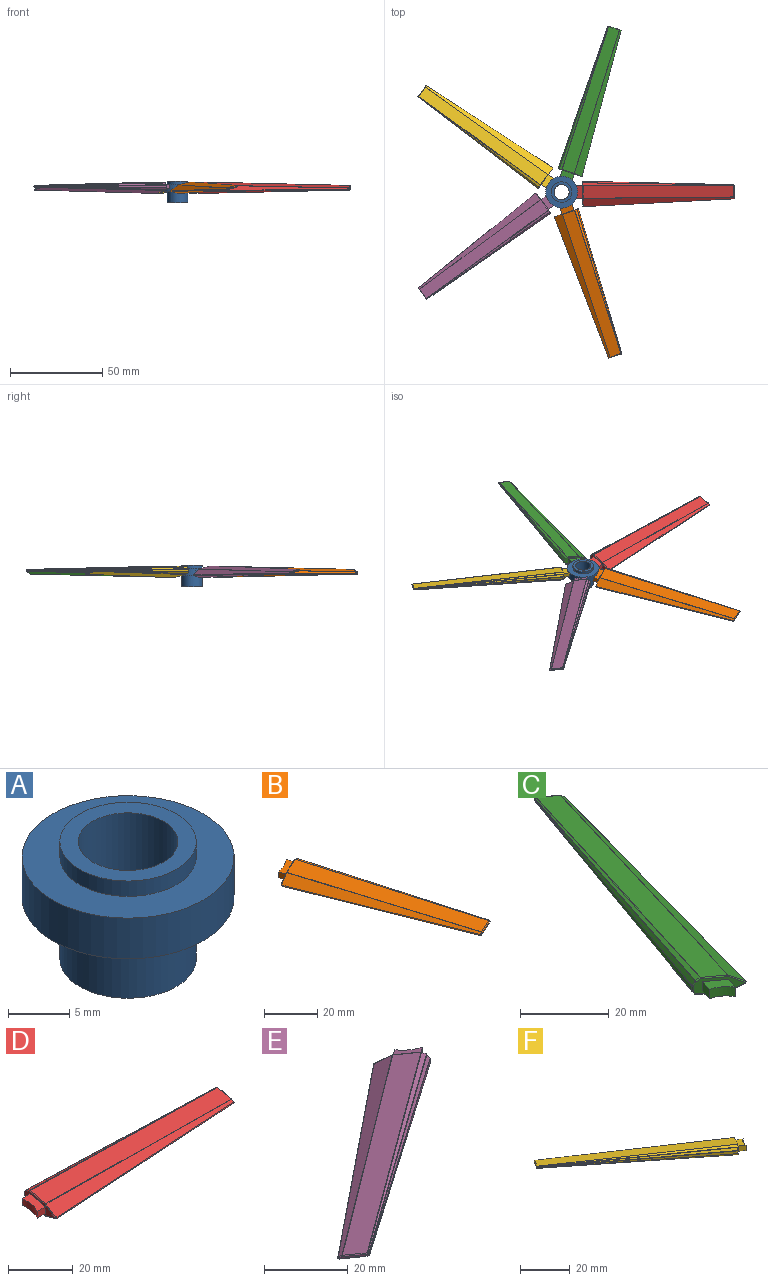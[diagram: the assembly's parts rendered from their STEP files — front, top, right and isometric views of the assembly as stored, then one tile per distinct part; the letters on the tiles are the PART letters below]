
ASSEMBLY  parts=6 mates=5
PART A: 8 faces, bbox 17.3x17.3x11.7 mm
  f0: cylinder r=5.56mm len=11.11mm, axis (0,0,-1), area 212.8mm2, adj f3,f6
  f1: cylinder r=5.56mm len=11.11mm, axis (0,0,-1), area 53.2mm2, adj f2,f7
  f2: plane 11.11x11.11mm, normal (0,0,1), area 45.1mm2, adj f1,f4
  f3: plane 11.11x11.11mm, normal (0,0,-1), area 45.1mm2, adj f0,f4
  f4: cylinder r=4.06mm len=11.68mm, axis (0,0,1), area 298.3mm2, adj f2,f3
  f5: cylinder r=8.64mm len=17.27mm, axis (0,0,1), area 220.5mm2, adj f6,f7
  f6: plane 17.27x17.27mm, normal (0,0,-1), area 137.3mm2, adj f0,f5
  f7: plane 17.27x17.27mm, normal (0,0,1), area 137.3mm2, adj f1,f5
PART B: 57 faces, bbox 36.5x83.4x6.3 mm
  f0: cylinder r=8.64mm len=6.36mm, axis (0,0,1), area 17.4mm2, adj f1,f2,f3,f4
  f1: plane 7.45x5.38mm, normal (-0.21,-0.07,0.97), area 20.7mm2, adj f0,f2,f4,f16
  f2: plane 3.3x2.54mm, normal (-0.95,-0.31,0), area 8.8mm2, adj f0,f1,f3,f16
  f3: plane 7.45x5.38mm, normal (0.21,0.07,-0.97), area 20.7mm2, adj f0,f2,f4,f16
  f4: plane 3.3x2.54mm, normal (0.95,0.31,0), area 8.8mm2, adj f0,f1,f3,f16
  f5: plane 78.08x25.36mm, normal (0.3,0.07,-0.95), area 81.9mm2, adj f19,f25,f28,f29
  f6: plane 78.11x24.21mm, normal (0.78,0.23,-0.59), area 55.6mm2, adj f18,f19,f21,f22
  f7: plane 78.09x23.5mm, normal (0.96,0.29,0), area 55.6mm2, adj f22,f23,f30,f31
  f8: plane 78.11x24.21mm, normal (0.78,0.23,0.59), area 55.6mm2, adj f31,f32,f37,f38
  f9: plane 77.94x25.3mm, normal (0.3,0.07,0.95), area 60.2mm2, adj f38,f39,f45,f46
  f10: plane 79.44x31.65mm, normal (-0.2,-0.09,0.97), area 540.6mm2, adj f46,f47,f51,f52
  f11: plane 77.59x29.99mm, normal (-0.53,-0.2,0.82), area 262.3mm2, adj f12,f41,f48,f52,f54
  f12: cone r=0.31mm half-angle=1.3deg, axis (-0.31,0.95,0), area 1.5mm2, adj f11,f13,f41,f55
  f13: plane 77.58x29.26mm, normal (-0.22,-0.1,-0.97), area 188.6mm2, adj f12,f14,f40,f41,f56
  f14: plane 79.73x31.38mm, normal (0.22,0.05,-0.97), area 564.5mm2, adj f13,f16,f25,f29,f36,f56
  f15: plane 6.84x2.22mm, normal (0.31,-0.95,0), area 3mm2, adj f18,f23,f28,f32,f36,f39,f40,f47
  f16: plane 12.51x5.82mm, normal (-0.31,0.95,0), area 27.8mm2, adj f1,f2,f3,f4,f14,f21,f25,f30
  f17: sphere r=0.25mm, area 0mm2, adj f18,f22,f23
  f18: cylinder r=0.25mm len=0.32mm, axis (-0.56,-0.18,-0.81), area 0mm2, adj f6,f15,f17,f24
  f19: cylinder r=0.25mm len=77.92mm, axis (-0.3,0.95,-0.02), area 13mm2, adj f5,f6,f20,f24
  f20: sphere r=0.25mm, area 0mm2, adj f19,f21,f25
  f21: cylinder r=0.25mm len=1.17mm, axis (0.56,0.18,0.81), area 0.5mm2, adj f6,f16,f20,f26
  f22: cylinder r=0.25mm len=78.11mm, axis (-0.29,0.96,-0.01), area 13mm2, adj f6,f7,f17,f26
  f23: cylinder r=0.25mm len=0.31mm, axis (0,0,-1), area 0mm2, adj f7,f15,f17,f27
  f24: sphere r=0.25mm, area 0mm2, adj f18,f19,f28
  f25: cylinder r=0.25mm len=3.97mm, axis (0.9,0.29,0.31), area 1mm2, adj f5,f14,f16,f20,f29
  f26: sphere r=0.25mm, area 0mm2, adj f21,f22,f30
  f27: sphere r=0.25mm, area 0mm2, adj f23,f31,f32
  f28: cylinder r=0.25mm len=0.64mm, axis (-0.9,-0.29,-0.31), area 0.3mm2, adj f5,f15,f24,f33
  f29: cylinder r=0.25mm len=77.72mm, axis (-0.3,0.95,-0.02), area 1.9mm2, adj f5,f14,f25,f33
  f30: cylinder r=0.25mm len=1.26mm, axis (0,0,1), area 0.5mm2, adj f7,f16,f26,f34
  f31: cylinder r=0.25mm len=78.11mm, axis (-0.29,0.96,0.01), area 13mm2, adj f7,f8,f27,f34
  f32: cylinder r=0.25mm len=0.32mm, axis (0.56,0.18,-0.81), area 0mm2, adj f8,f15,f27,f35
  f33: sphere r=0.25mm, area 0mm2, adj f28,f29,f36
  f34: sphere r=0.25mm, area 0mm2, adj f30,f31,f37
  f35: sphere r=0.25mm, area 0mm2, adj f32,f38,f39
  f36: cylinder r=0.25mm len=6.21mm, axis (0.93,0.3,0.22), area 2.6mm2, adj f14,f15,f33,f40
  f37: cylinder r=0.25mm len=1.17mm, axis (-0.56,-0.18,0.81), area 0.5mm2, adj f8,f16,f34,f42
  f38: cylinder r=0.25mm len=77.92mm, axis (-0.3,0.95,0.02), area 13mm2, adj f8,f9,f35,f42
  f39: cylinder r=0.25mm len=0.32mm, axis (0.9,0.29,-0.31), area 0.1mm2, adj f9,f15,f35,f43
  f40: cylinder r=0.25mm len=0.28mm, axis (0.92,0.3,-0.24), area 0mm2, adj f13,f15,f36,f44
  f41: cylinder r=0.25mm len=74.06mm, axis (-0.36,0.93,-0.01), area 46.2mm2, adj f11,f12,f13,f44
  f42: sphere r=0.25mm, area 0mm2, adj f37,f38,f45
  f43: sphere r=0.25mm, area 0mm2, adj f39,f46,f47
  f44: sphere r=0.25mm, area 0.1mm2, adj f40,f41,f48
  f45: cylinder r=0.25mm len=1.31mm, axis (-0.9,-0.29,0.31), area 0.5mm2, adj f9,f16,f42,f49
  f46: cylinder r=0.25mm len=77.61mm, axis (-0.31,0.95,0.02), area 11.1mm2, adj f9,f10,f43,f49
  f47: cylinder r=0.25mm len=5.89mm, axis (-0.93,-0.3,-0.22), area 2.4mm2, adj f10,f15,f43,f50
  f48: cylinder r=0.25mm len=1.06mm, axis (-0.78,-0.25,-0.57), area 0.4mm2, adj f11,f15,f44,f50
  f49: sphere r=0.25mm, area 0mm2, adj f45,f46,f51
  f50: sphere r=0.25mm, area 0mm2, adj f47,f48,f52
  f51: cylinder r=0.25mm len=6.58mm, axis (0.93,0.3,0.22), area 2.8mm2, adj f10,f16,f49,f53
  f52: cylinder r=0.25mm len=77.35mm, axis (-0.32,0.95,0.02), area 7.9mm2, adj f10,f11,f50,f53
  f53: sphere r=0.25mm, area 0mm2, adj f51,f52,f54
  f54: cylinder r=0.25mm len=4.18mm, axis (0.78,0.25,0.57), area 2.1mm2, adj f11,f16,f53,f55
  f55: torus R=0.05mm, axis (0.31,-0.95,0), area 0.2mm2, adj f12,f16,f54,f56
  f56: cylinder r=0.25mm len=4.56mm, axis (-0.92,-0.3,0.24), area 1.8mm2, adj f13,f14,f16,f55
PART C: 57 faces, bbox 34.3x83.6x6.3 mm
  f0: cylinder r=8.64mm len=6.36mm, axis (0,0,1), area 17.4mm2, adj f1,f2,f3,f4
  f1: plane 7.45x5.38mm, normal (0.21,-0.07,0.97), area 20.7mm2, adj f0,f2,f4,f16
  f2: plane 3.3x2.54mm, normal (0.95,-0.31,0), area 8.8mm2, adj f0,f1,f3,f16
  f3: plane 7.45x5.38mm, normal (-0.21,0.07,-0.97), area 20.7mm2, adj f0,f2,f4,f16
  f4: plane 3.3x2.54mm, normal (-0.95,0.31,0), area 8.8mm2, adj f0,f1,f3,f16
  f5: plane 77.6x26.85mm, normal (-0.29,0.12,-0.95), area 81.9mm2, adj f19,f25,f28,f29
  f6: plane 77.22x26.95mm, normal (-0.76,0.27,-0.59), area 55.6mm2, adj f18,f19,f21,f22
  f7: plane 76.99x26.89mm, normal (-0.94,0.33,0), area 55.6mm2, adj f22,f23,f30,f31
  f8: plane 77.22x26.95mm, normal (-0.76,0.27,0.59), area 55.6mm2, adj f31,f32,f37,f38
  f9: plane 77.58x26.43mm, normal (-0.29,0.12,0.95), area 60.2mm2, adj f38,f39,f45,f46
  f10: plane 79.64x31.03mm, normal (0.22,-0.05,0.97), area 540.6mm2, adj f46,f47,f51,f52
  f11: plane 79.1x25.34mm, normal (0.55,-0.15,0.82), area 262.3mm2, adj f12,f41,f48,f52,f54
  f12: cone r=0.31mm half-angle=1.3deg, axis (-0.31,-0.95,0), area 1.5mm2, adj f11,f13,f41,f55
  f13: plane 78.86x25.3mm, normal (0.24,-0.05,-0.97), area 188.6mm2, adj f12,f14,f40,f41,f56
  f14: plane 79.68x31.82mm, normal (-0.2,0.09,-0.97), area 564.5mm2, adj f13,f16,f25,f29,f36,f56
  f15: plane 6.84x2.22mm, normal (0.31,0.95,0), area 3mm2, adj f18,f23,f28,f32,f36,f39,f40,f47
  f16: plane 12.51x5.82mm, normal (-0.31,-0.95,0), area 27.8mm2, adj f1,f2,f3,f4,f14,f21,f25,f30
  f17: sphere r=0.25mm, area 0mm2, adj f18,f22,f23
  f18: cylinder r=0.25mm len=0.33mm, axis (0.56,-0.18,-0.81), area 0mm2, adj f6,f15,f17,f24
  f19: cylinder r=0.25mm len=77.24mm, axis (-0.32,-0.95,-0.02), area 13mm2, adj f5,f6,f20,f24
  f20: sphere r=0.25mm, area 0mm2, adj f19,f21,f25
  f21: cylinder r=0.25mm len=1.17mm, axis (-0.56,0.18,0.81), area 0.5mm2, adj f6,f16,f20,f26
  f22: cylinder r=0.25mm len=77.01mm, axis (-0.33,-0.94,-0.01), area 13mm2, adj f6,f7,f17,f26
  f23: cylinder r=0.25mm len=0.32mm, axis (0,0,-1), area 0mm2, adj f7,f15,f17,f27
  f24: sphere r=0.25mm, area 0mm2, adj f18,f19,f28
  f25: cylinder r=0.25mm len=3.85mm, axis (-0.9,0.29,0.31), area 1mm2, adj f5,f14,f16,f20,f29
  f26: sphere r=0.25mm, area 0mm2, adj f21,f22,f30
  f27: sphere r=0.25mm, area 0mm2, adj f23,f31,f32
  f28: cylinder r=0.25mm len=0.76mm, axis (0.9,-0.29,-0.31), area 0.3mm2, adj f5,f15,f24,f33
  f29: cylinder r=0.25mm len=77.43mm, axis (-0.31,-0.95,-0.02), area 1.9mm2, adj f5,f14,f25,f33
  f30: cylinder r=0.25mm len=1.26mm, axis (0,0,1), area 0.5mm2, adj f7,f16,f26,f34
  f31: cylinder r=0.25mm len=77.01mm, axis (-0.33,-0.94,0.01), area 13mm2, adj f7,f8,f27,f34
  f32: cylinder r=0.25mm len=0.33mm, axis (-0.56,0.18,-0.81), area 0mm2, adj f8,f15,f27,f35
  f33: sphere r=0.25mm, area 0mm2, adj f28,f29,f36
  f34: sphere r=0.25mm, area 0mm2, adj f30,f31,f37
  f35: sphere r=0.25mm, area 0mm2, adj f32,f38,f39
  f36: cylinder r=0.25mm len=6.3mm, axis (-0.93,0.3,0.22), area 2.6mm2, adj f14,f15,f33,f40
  f37: cylinder r=0.25mm len=1.17mm, axis (0.56,-0.18,0.81), area 0.5mm2, adj f8,f16,f34,f42
  f38: cylinder r=0.25mm len=77.24mm, axis (-0.32,-0.95,0.02), area 13mm2, adj f8,f9,f35,f42
  f39: cylinder r=0.25mm len=0.34mm, axis (-0.9,0.29,-0.31), area 0.1mm2, adj f9,f15,f35,f43
  f40: cylinder r=0.25mm len=0.29mm, axis (-0.92,0.3,-0.24), area 0mm2, adj f13,f15,f36,f44
  f41: cylinder r=0.25mm len=76.6mm, axis (-0.26,-0.97,-0.01), area 46.2mm2, adj f11,f12,f13,f44
  f42: sphere r=0.25mm, area 0mm2, adj f37,f38,f45
  f43: sphere r=0.25mm, area 0mm2, adj f39,f46,f47
  f44: sphere r=0.25mm, area 0.1mm2, adj f40,f41,f48
  f45: cylinder r=0.25mm len=1.19mm, axis (0.9,-0.29,0.31), area 0.5mm2, adj f9,f16,f42,f49
  f46: cylinder r=0.25mm len=77.56mm, axis (-0.31,-0.95,0.02), area 11.1mm2, adj f9,f10,f43,f49
  f47: cylinder r=0.25mm len=5.8mm, axis (0.93,-0.3,-0.22), area 2.4mm2, adj f10,f15,f43,f50
  f48: cylinder r=0.25mm len=0.92mm, axis (0.78,-0.25,-0.57), area 0.4mm2, adj f11,f15,f44,f50
  f49: sphere r=0.25mm, area 0mm2, adj f45,f46,f51
  f50: sphere r=0.25mm, area 0mm2, adj f47,f48,f52
  f51: cylinder r=0.25mm len=6.67mm, axis (-0.93,0.3,0.22), area 2.8mm2, adj f10,f16,f49,f53
  f52: cylinder r=0.25mm len=77.8mm, axis (-0.3,-0.95,0.02), area 7.9mm2, adj f10,f11,f50,f53
  f53: sphere r=0.25mm, area 0mm2, adj f51,f52,f54
  f54: cylinder r=0.25mm len=4.32mm, axis (-0.78,0.25,0.57), area 2.1mm2, adj f11,f16,f53,f55
  f55: torus R=0.05mm, axis (0.31,0.95,0), area 0.2mm2, adj f12,f16,f54,f56
  f56: cylinder r=0.25mm len=4.66mm, axis (0.92,-0.3,0.24), area 1.8mm2, adj f13,f14,f16,f55
PART D: 57 faces, bbox 85.5x13.7x6.3 mm
  f0: cylinder r=8.64mm len=6.69mm, axis (0,0,1), area 17.4mm2, adj f1,f2,f3,f4
  f1: plane 6.7x3.48mm, normal (0,-0.22,0.97), area 20.7mm2, adj f0,f2,f4,f16
  f2: plane 3.47x2.54mm, normal (0,-1,0), area 8.8mm2, adj f0,f1,f3,f16
  f3: plane 6.7x3.48mm, normal (0,0.22,-0.97), area 20.7mm2, adj f0,f2,f4,f16
  f4: plane 3.47x2.54mm, normal (0,1,0), area 8.8mm2, adj f0,f1,f3,f16
  f5: plane 81.53x1.93mm, normal (0.02,0.31,-0.95), area 81.9mm2, adj f19,f25,f28,f29
  f6: plane 81.53x1.84mm, normal (0.02,0.81,-0.59), area 55.6mm2, adj f18,f19,f21,f22
  f7: plane 81.53x1.78mm, normal (0.02,1,0), area 55.6mm2, adj f22,f23,f30,f31
  f8: plane 81.53x1.84mm, normal (0.02,0.81,0.59), area 55.6mm2, adj f31,f32,f37,f38
  f9: plane 81.53x1.91mm, normal (0.02,0.31,0.95), area 60.2mm2, adj f38,f39,f45,f46
  f10: plane 81.53x6.87mm, normal (0.02,-0.22,0.97), area 540.6mm2, adj f46,f47,f51,f52
  f11: plane 81.53x5.04mm, normal (0.02,-0.57,0.82), area 262.3mm2, adj f12,f41,f48,f52,f54
  f12: cone r=0.31mm half-angle=1.3deg, axis (-1,0,0), area 1.5mm2, adj f11,f13,f41,f55
  f13: plane 81.53x4.27mm, normal (0.02,-0.24,-0.97), area 188.6mm2, adj f12,f14,f40,f41,f56
  f14: plane 81.79x6.97mm, normal (0.02,0.22,-0.97), area 564.5mm2, adj f13,f16,f25,f29,f36,f56
  f15: plane 7.2x2.01mm, normal (1,0,0), area 3mm2, adj f18,f23,f28,f32,f36,f39,f40,f47
  f16: plane 13.16x5.82mm, normal (-1,0,0), area 27.8mm2, adj f1,f2,f3,f4,f14,f21,f25,f30
  f17: sphere r=0.25mm, area 0mm2, adj f18,f22,f23
  f18: cylinder r=0.25mm len=0.27mm, axis (0,-0.59,-0.81), area 0mm2, adj f6,f15,f17,f24
  f19: cylinder r=0.25mm len=81.53mm, axis (-1,0.01,-0.02), area 13mm2, adj f5,f6,f20,f24
  f20: sphere r=0.25mm, area 0mm2, adj f19,f21,f25
  f21: cylinder r=0.25mm len=1.17mm, axis (0,0.59,0.81), area 0.5mm2, adj f6,f16,f20,f26
  f22: cylinder r=0.25mm len=81.53mm, axis (-1,0.02,-0.01), area 13mm2, adj f6,f7,f17,f26
  f23: cylinder r=0.25mm len=0.25mm, axis (0,0,-1), area 0mm2, adj f7,f15,f17,f27
  f24: sphere r=0.25mm, area 0mm2, adj f18,f19,f28
  f25: cylinder r=0.25mm len=4.09mm, axis (0,0.95,0.31), area 1mm2, adj f5,f14,f16,f20,f29
  f26: sphere r=0.25mm, area 0mm2, adj f21,f22,f30
  f27: sphere r=0.25mm, area 0mm2, adj f23,f31,f32
  f28: cylinder r=0.25mm len=0.72mm, axis (0,-0.95,-0.31), area 0.3mm2, adj f5,f15,f24,f33
  f29: cylinder r=0.25mm len=81.56mm, axis (-1,0.01,-0.02), area 1.9mm2, adj f5,f14,f25,f33
  f30: cylinder r=0.25mm len=1.26mm, axis (0,0,1), area 0.5mm2, adj f7,f16,f26,f34
  f31: cylinder r=0.25mm len=81.53mm, axis (-1,0.02,0.01), area 13mm2, adj f7,f8,f27,f34
  f32: cylinder r=0.25mm len=0.27mm, axis (0,0.59,-0.81), area 0mm2, adj f8,f15,f27,f35
  f33: sphere r=0.25mm, area 0mm2, adj f28,f29,f36
  f34: sphere r=0.25mm, area 0mm2, adj f30,f31,f37
  f35: sphere r=0.25mm, area 0mm2, adj f32,f38,f39
  f36: cylinder r=0.25mm len=6.54mm, axis (0,0.97,0.22), area 2.6mm2, adj f14,f15,f33,f40
  f37: cylinder r=0.25mm len=1.17mm, axis (0,-0.59,0.81), area 0.5mm2, adj f8,f16,f34,f42
  f38: cylinder r=0.25mm len=81.53mm, axis (-1,0.01,0.02), area 13mm2, adj f8,f9,f35,f42
  f39: cylinder r=0.25mm len=0.3mm, axis (0,0.95,-0.31), area 0.1mm2, adj f9,f15,f35,f43
  f40: cylinder r=0.25mm len=0.28mm, axis (0,0.97,-0.24), area 0mm2, adj f13,f15,f36,f44
  f41: cylinder r=0.25mm len=79.15mm, axis (-1,-0.05,-0.01), area 46.2mm2, adj f11,f12,f13,f44
  f42: sphere r=0.25mm, area 0mm2, adj f37,f38,f45
  f43: sphere r=0.25mm, area 0mm2, adj f39,f46,f47
  f44: sphere r=0.25mm, area 0.1mm2, adj f40,f41,f48
  f45: cylinder r=0.25mm len=1.29mm, axis (0,-0.95,0.31), area 0.5mm2, adj f9,f16,f42,f49
  f46: cylinder r=0.25mm len=81.53mm, axis (-1,0,0.02), area 11.1mm2, adj f9,f10,f43,f49
  f47: cylinder r=0.25mm len=6.11mm, axis (0,-0.97,-0.22), area 2.4mm2, adj f10,f15,f43,f50
  f48: cylinder r=0.25mm len=1.03mm, axis (0,-0.82,-0.57), area 0.4mm2, adj f11,f15,f44,f50
  f49: sphere r=0.25mm, area 0mm2, adj f45,f46,f51
  f50: sphere r=0.25mm, area 0mm2, adj f47,f48,f52
  f51: cylinder r=0.25mm len=6.93mm, axis (0,0.97,0.22), area 2.8mm2, adj f10,f16,f49,f53
  f52: cylinder r=0.25mm len=81.53mm, axis (-1,-0.01,0.02), area 7.9mm2, adj f10,f11,f50,f53
  f53: sphere r=0.25mm, area 0mm2, adj f51,f52,f54
  f54: cylinder r=0.25mm len=4.46mm, axis (0,0.82,0.57), area 2.1mm2, adj f11,f16,f53,f55
  f55: torus R=0.05mm, axis (1,0,0), area 0.2mm2, adj f12,f16,f54,f56
  f56: cylinder r=0.25mm len=4.82mm, axis (0,-0.97,0.24), area 1.8mm2, adj f13,f14,f16,f55
PART E: 57 faces, bbox 73.2x57.7x6.3 mm
  f0: cylinder r=8.64mm len=5.41mm, axis (0,0,1), area 17.4mm2, adj f1,f2,f3,f4
  f1: plane 7.46x6.75mm, normal (-0.13,0.18,0.97), area 20.7mm2, adj f0,f2,f4,f16
  f2: plane 2.81x2.54mm, normal (-0.59,0.81,0), area 8.8mm2, adj f0,f1,f3,f16
  f3: plane 7.46x6.75mm, normal (0.13,-0.18,-0.97), area 20.7mm2, adj f0,f2,f4,f16
  f4: plane 2.81x2.54mm, normal (0.59,-0.81,0), area 8.8mm2, adj f0,f1,f3,f16
  f5: plane 66.99x48.06mm, normal (0.16,-0.26,-0.95), area 81.9mm2, adj f19,f25,f28,f29
  f6: plane 67.04x47.08mm, normal (0.46,-0.67,-0.59), area 55.6mm2, adj f18,f19,f21,f22
  f7: plane 67.01x46.49mm, normal (0.57,-0.82,0), area 55.6mm2, adj f22,f23,f30,f31
  f8: plane 67.04x47.08mm, normal (0.46,-0.67,0.59), area 55.6mm2, adj f31,f32,f37,f38
  f9: plane 66.72x48.01mm, normal (0.16,-0.26,0.95), area 60.2mm2, adj f38,f39,f45,f46
  f10: plane 69.57x53.41mm, normal (-0.15,0.17,0.97), area 540.6mm2, adj f46,f47,f51,f52
  f11: plane 66.05x52.01mm, normal (-0.35,0.45,0.82), area 262.3mm2, adj f12,f41,f48,f52,f54
  f12: cone r=0.31mm half-angle=1.3deg, axis (0.81,0.59,0), area 1.5mm2, adj f11,f13,f41,f55
  f13: plane 66.03x51.38mm, normal (-0.16,0.18,-0.97), area 188.6mm2, adj f12,f14,f40,f41,f56
  f14: plane 70.07x53.21mm, normal (0.11,-0.19,-0.97), area 564.5mm2, adj f13,f16,f25,f29,f36,f56
  f15: plane 5.82x4.23mm, normal (-0.81,-0.59,0), area 3mm2, adj f18,f23,f28,f32,f36,f39,f40,f47
  f16: plane 10.65x7.73mm, normal (0.81,0.59,0), area 27.8mm2, adj f1,f2,f3,f4,f14,f21,f25,f30
  f17: sphere r=0.25mm, area 0mm2, adj f18,f22,f23
  f18: cylinder r=0.25mm len=0.36mm, axis (-0.35,0.48,-0.81), area 0mm2, adj f6,f15,f17,f24
  f19: cylinder r=0.25mm len=66.68mm, axis (0.82,0.58,-0.02), area 13mm2, adj f5,f6,f20,f24
  f20: sphere r=0.25mm, area 0mm2, adj f19,f21,f25
  f21: cylinder r=0.25mm len=1.17mm, axis (0.35,-0.48,0.81), area 0.5mm2, adj f6,f16,f20,f26
  f22: cylinder r=0.25mm len=67.04mm, axis (0.82,0.57,-0.01), area 13mm2, adj f6,f7,f17,f26
  f23: cylinder r=0.25mm len=0.35mm, axis (0,0,-1), area 0mm2, adj f7,f15,f17,f27
  f24: sphere r=0.25mm, area 0mm2, adj f18,f19,f28
  f25: cylinder r=0.25mm len=3.46mm, axis (0.56,-0.77,0.31), area 1mm2, adj f5,f14,f16,f20,f29
  f26: sphere r=0.25mm, area 0mm2, adj f21,f22,f30
  f27: sphere r=0.25mm, area 0mm2, adj f23,f31,f32
  f28: cylinder r=0.25mm len=0.62mm, axis (-0.56,0.77,-0.31), area 0.3mm2, adj f5,f15,f24,f33
  f29: cylinder r=0.25mm len=66.27mm, axis (0.81,0.58,-0.02), area 1.9mm2, adj f5,f14,f25,f33
  f30: cylinder r=0.25mm len=1.26mm, axis (0,0,1), area 0.5mm2, adj f7,f16,f26,f34
  f31: cylinder r=0.25mm len=67.04mm, axis (0.82,0.57,0.01), area 13mm2, adj f7,f8,f27,f34
  f32: cylinder r=0.25mm len=0.36mm, axis (0.35,-0.48,-0.81), area 0mm2, adj f8,f15,f27,f35
  f33: sphere r=0.25mm, area 0mm2, adj f28,f29,f36
  f34: sphere r=0.25mm, area 0mm2, adj f30,f31,f37
  f35: sphere r=0.25mm, area 0mm2, adj f32,f38,f39
  f36: cylinder r=0.25mm len=5.35mm, axis (0.57,-0.79,0.22), area 2.6mm2, adj f14,f15,f33,f40
  f37: cylinder r=0.25mm len=1.17mm, axis (-0.35,0.48,0.81), area 0.5mm2, adj f8,f16,f34,f42
  f38: cylinder r=0.25mm len=66.68mm, axis (0.82,0.58,0.02), area 13mm2, adj f8,f9,f35,f42
  f39: cylinder r=0.25mm len=0.36mm, axis (0.56,-0.77,-0.31), area 0.1mm2, adj f9,f15,f35,f43
  f40: cylinder r=0.25mm len=0.3mm, axis (0.57,-0.79,-0.24), area 0mm2, adj f13,f15,f36,f44
  f41: cylinder r=0.25mm len=61.72mm, axis (0.78,0.63,-0.01), area 46.2mm2, adj f11,f12,f13,f44
  f42: sphere r=0.25mm, area 0mm2, adj f37,f38,f45
  f43: sphere r=0.25mm, area 0mm2, adj f39,f46,f47
  f44: sphere r=0.25mm, area 0.1mm2, adj f40,f41,f48
  f45: cylinder r=0.25mm len=1.2mm, axis (-0.56,0.77,0.31), area 0.5mm2, adj f9,f16,f42,f49
  f46: cylinder r=0.25mm len=66.09mm, axis (0.81,0.59,0.02), area 11.1mm2, adj f9,f10,f43,f49
  f47: cylinder r=0.25mm len=5.09mm, axis (-0.57,0.79,-0.22), area 2.4mm2, adj f10,f15,f43,f50
  f48: cylinder r=0.25mm len=0.98mm, axis (-0.48,0.67,-0.57), area 0.4mm2, adj f11,f15,f44,f50
  f49: sphere r=0.25mm, area 0mm2, adj f45,f46,f51
  f50: sphere r=0.25mm, area 0mm2, adj f47,f48,f52
  f51: cylinder r=0.25mm len=5.67mm, axis (0.57,-0.79,0.22), area 2.8mm2, adj f10,f16,f49,f53
  f52: cylinder r=0.25mm len=65.59mm, axis (0.8,0.59,0.02), area 7.9mm2, adj f10,f11,f50,f53
  f53: sphere r=0.25mm, area 0mm2, adj f51,f52,f54
  f54: cylinder r=0.25mm len=3.57mm, axis (0.48,-0.67,0.57), area 2.1mm2, adj f11,f16,f53,f55
  f55: torus R=0.05mm, axis (-0.81,-0.59,0), area 0.2mm2, adj f12,f16,f54,f56
  f56: cylinder r=0.25mm len=3.96mm, axis (-0.57,0.79,0.24), area 1.8mm2, adj f13,f14,f16,f55
PART F: 57 faces, bbox 73.4x55.8x6.3 mm
  f0: cylinder r=8.64mm len=5.41mm, axis (0,0,1), area 17.4mm2, adj f1,f2,f3,f4
  f1: plane 7.46x6.75mm, normal (0.13,0.18,0.97), area 20.7mm2, adj f0,f2,f4,f16
  f2: plane 2.81x2.54mm, normal (0.59,0.81,0), area 8.8mm2, adj f0,f1,f3,f16
  f3: plane 7.46x6.75mm, normal (-0.13,-0.18,-0.97), area 20.7mm2, adj f0,f2,f4,f16
  f4: plane 2.81x2.54mm, normal (-0.59,-0.81,0), area 8.8mm2, adj f0,f1,f3,f16
  f5: plane 66.06x49.33mm, normal (-0.2,-0.24,-0.95), area 81.9mm2, adj f19,f25,f28,f29
  f6: plane 65.35x49.41mm, normal (-0.49,-0.64,-0.59), area 55.6mm2, adj f18,f19,f21,f22
  f7: plane 64.92x49.36mm, normal (-0.61,-0.8,0), area 55.6mm2, adj f22,f23,f30,f31
  f8: plane 65.35x49.41mm, normal (-0.49,-0.64,0.59), area 55.6mm2, adj f31,f32,f37,f38
  f9: plane 66.03x48.97mm, normal (-0.2,-0.24,0.95), area 60.2mm2, adj f38,f39,f45,f46
  f10: plane 69.95x52.89mm, normal (0.11,0.19,0.97), area 540.6mm2, adj f46,f47,f51,f52
  f11: plane 68.93x48.05mm, normal (0.32,0.47,0.82), area 262.3mm2, adj f12,f41,f48,f52,f54
  f12: cone r=0.31mm half-angle=1.3deg, axis (0.81,-0.59,0), area 1.5mm2, adj f11,f13,f41,f55
  f13: plane 68.47x48.01mm, normal (0.12,0.21,-0.97), area 188.6mm2, adj f12,f14,f40,f41,f56
  f14: plane 69.84x53.57mm, normal (-0.15,-0.17,-0.97), area 564.5mm2, adj f13,f16,f25,f29,f36,f56
  f15: plane 5.82x4.23mm, normal (-0.81,0.59,0), area 3mm2, adj f18,f23,f28,f32,f36,f39,f40,f47
  f16: plane 10.65x7.73mm, normal (0.81,-0.59,0), area 27.8mm2, adj f1,f2,f3,f4,f14,f21,f25,f30
  f17: sphere r=0.25mm, area 0mm2, adj f18,f22,f23
  f18: cylinder r=0.25mm len=0.36mm, axis (0.35,0.48,-0.81), area 0mm2, adj f6,f15,f17,f24
  f19: cylinder r=0.25mm len=65.39mm, axis (0.8,-0.6,-0.02), area 13mm2, adj f5,f6,f20,f24
  f20: sphere r=0.25mm, area 0mm2, adj f19,f21,f25
  f21: cylinder r=0.25mm len=1.17mm, axis (-0.35,-0.48,0.81), area 0.5mm2, adj f6,f16,f20,f26
  f22: cylinder r=0.25mm len=64.95mm, axis (0.8,-0.61,-0.01), area 13mm2, adj f6,f7,f17,f26
  f23: cylinder r=0.25mm len=0.35mm, axis (0,0,-1), area 0mm2, adj f7,f15,f17,f27
  f24: sphere r=0.25mm, area 0mm2, adj f18,f19,f28
  f25: cylinder r=0.25mm len=3.35mm, axis (-0.56,-0.77,0.31), area 1mm2, adj f5,f14,f16,f20,f29
  f26: sphere r=0.25mm, area 0mm2, adj f21,f22,f30
  f27: sphere r=0.25mm, area 0mm2, adj f23,f31,f32
  f28: cylinder r=0.25mm len=0.73mm, axis (0.56,0.77,-0.31), area 0.3mm2, adj f5,f15,f24,f33
  f29: cylinder r=0.25mm len=65.72mm, axis (0.81,-0.59,-0.02), area 1.9mm2, adj f5,f14,f25,f33
  f30: cylinder r=0.25mm len=1.26mm, axis (0,0,1), area 0.5mm2, adj f7,f16,f26,f34
  f31: cylinder r=0.25mm len=64.95mm, axis (0.8,-0.61,0.01), area 13mm2, adj f7,f8,f27,f34
  f32: cylinder r=0.25mm len=0.36mm, axis (-0.35,-0.48,-0.81), area 0mm2, adj f8,f15,f27,f35
  f33: sphere r=0.25mm, area 0mm2, adj f28,f29,f36
  f34: sphere r=0.25mm, area 0mm2, adj f30,f31,f37
  f35: sphere r=0.25mm, area 0mm2, adj f32,f38,f39
  f36: cylinder r=0.25mm len=5.44mm, axis (-0.57,-0.79,0.22), area 2.6mm2, adj f14,f15,f33,f40
  f37: cylinder r=0.25mm len=1.17mm, axis (0.35,0.48,0.81), area 0.5mm2, adj f8,f16,f34,f42
  f38: cylinder r=0.25mm len=65.39mm, axis (0.8,-0.6,0.02), area 13mm2, adj f8,f9,f35,f42
  f39: cylinder r=0.25mm len=0.37mm, axis (-0.56,-0.77,-0.31), area 0.1mm2, adj f9,f15,f35,f43
  f40: cylinder r=0.25mm len=0.31mm, axis (-0.57,-0.79,-0.24), area 0mm2, adj f13,f15,f36,f44
  f41: cylinder r=0.25mm len=66.56mm, axis (0.84,-0.54,-0.01), area 46.2mm2, adj f11,f12,f13,f44
  f42: sphere r=0.25mm, area 0mm2, adj f37,f38,f45
  f43: sphere r=0.25mm, area 0mm2, adj f39,f46,f47
  f44: sphere r=0.25mm, area 0.1mm2, adj f40,f41,f48
  f45: cylinder r=0.25mm len=1.08mm, axis (0.56,0.77,0.31), area 0.5mm2, adj f9,f16,f42,f49
  f46: cylinder r=0.25mm len=65.99mm, axis (0.81,-0.59,0.02), area 11.1mm2, adj f9,f10,f43,f49
  f47: cylinder r=0.25mm len=5.01mm, axis (0.57,0.79,-0.22), area 2.4mm2, adj f10,f15,f43,f50
  f48: cylinder r=0.25mm len=0.82mm, axis (0.48,0.67,-0.57), area 0.4mm2, adj f11,f15,f44,f50
  f49: sphere r=0.25mm, area 0mm2, adj f45,f46,f51
  f50: sphere r=0.25mm, area 0mm2, adj f47,f48,f52
  f51: cylinder r=0.25mm len=5.76mm, axis (-0.57,-0.79,0.22), area 2.8mm2, adj f10,f16,f49,f53
  f52: cylinder r=0.25mm len=66.44mm, axis (0.81,-0.58,0.02), area 7.9mm2, adj f10,f11,f50,f53
  f53: sphere r=0.25mm, area 0mm2, adj f51,f52,f54
  f54: cylinder r=0.25mm len=3.76mm, axis (-0.48,-0.67,0.57), area 2.1mm2, adj f11,f16,f53,f55
  f55: torus R=0.05mm, axis (-0.81,0.59,0), area 0.2mm2, adj f12,f16,f54,f56
  f56: cylinder r=0.25mm len=4.05mm, axis (0.57,0.79,0.24), area 1.8mm2, adj f13,f14,f16,f55
PLACE A at identity
PLACE B at identity
PLACE C at identity
PLACE D at identity
PLACE E at identity
PLACE F at identity
MATE fastened A.f0 <-> E.f0  axis (0,0,1) through (0,0,8.13)mm
MATE fastened A.f0 <-> B.f0  axis (0,0,1) through (0,0,8.13)mm
MATE fastened A.f0 <-> F.f0  axis (0,0,1) through (0,0,8.13)mm
MATE fastened A.f0 <-> D.f0  axis (0,0,1) through (0,0,8.13)mm
MATE fastened A.f0 <-> C.f0  axis (0,0,1) through (0,0,8.13)mm
